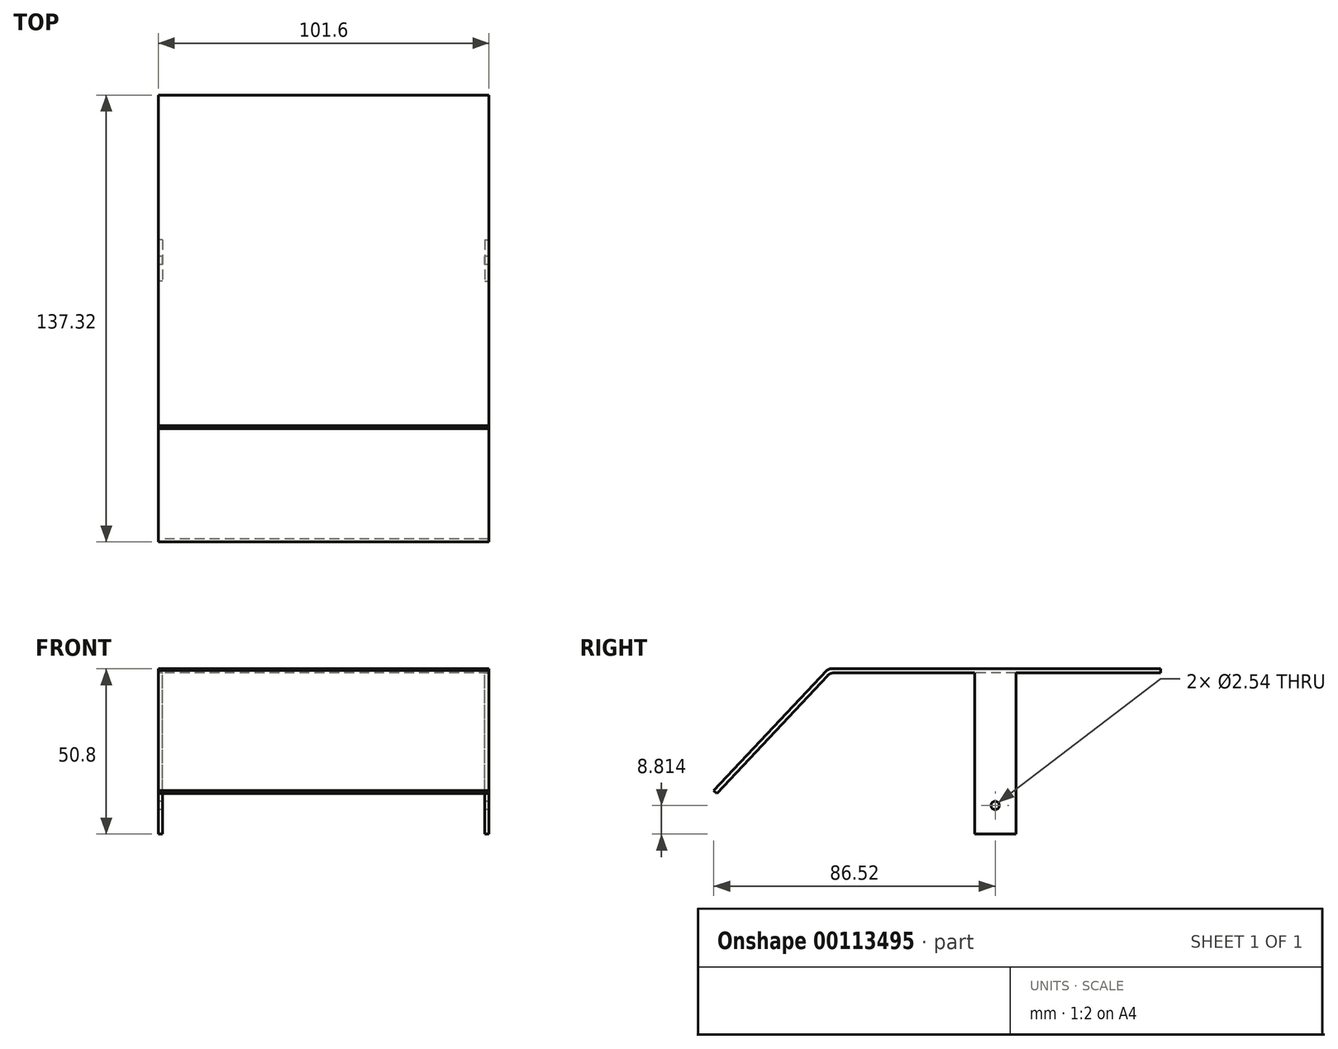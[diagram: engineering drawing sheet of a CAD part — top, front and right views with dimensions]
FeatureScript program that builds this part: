
annotation { "Feature Type Name" : "Feature", "Feature Type Description" : "" }
export const myFeature = defineFeature(function(context is Context, id is Id, definition is map)
    precondition{}
    {
        {
            var Q0;
            Q0=qCreatedBy(makeId("Top.planeOp"),FACE);
            var sketch = newSketch(context, id + "F0", { "sketchPlane" : qUnion([Q0])});
            skLineSegment(sketch, "E0.bottom", {"start": v(50.8, 50.8) * mm, "end": v(-50.8, 50.8) * mm});
            skLineSegment(sketch, "E0.top", {"start": v(50.8, -50.8) * mm, "end": v(-50.8, -50.8) * mm});
            skLineSegment(sketch, "E0.left", {"start": v(50.8, 50.8) * mm, "end": v(50.8, -50.8) * mm});
            skLineSegment(sketch, "E0.right", {"start": v(-50.8, 50.8) * mm, "end": v(-50.8, -50.8) * mm});
            skPoint(sketch, "E0.middle", {"position": v(0, 0) * mm});
            skSolve(sketch);
        }
        {
            var Q0;
            Q0=makeQuery(id+"F0.imprint","IMPRINT",FACE,{"disambiguationData":[TD([[makeQuery(id+"F0.imprint","IMPRINT",EDGE,{"derivedFrom":sQuery(id+"F0.wireOp",EDGE,"E0.bottom")}),1.0]])]});
            extrude(context, id + "F1", {"entities" : qUnion([Q0]), "depth" : 1.27 * mm});
        }
        {
            var Q0;
            Q0=qCreatedBy(makeId("Right.planeOp"),FACE);
            var sketch = newSketch(context, id + "F2", { "sketchPlane" : qUnion([Q0])});
            skLineSegment(sketch, "E1", {"start": v(-50.8, 0) * mm, "end": v(-85.6, -37.01) * mm});
            skLineSegment(sketch, "E2", {"start": v(-68.2, -18.5) * mm, "end": v(-69.12, -17.64) * mm});
            skLineSegment(sketch, "E3", {"start": v(-50.8, 0) * mm, "end": v(-51.73, 0.87) * mm});
            skLineSegment(sketch, "E4", {"start": v(-85.6, -37.01) * mm, "end": v(-86.52, -36.14) * mm});
            skLineSegment(sketch, "E5", {"start": v(-51.73, 0.87) * mm, "end": v(-86.52, -36.14) * mm});
            skLineSegment(sketch, "E6", {"start": v(-51.73, 0.87) * mm, "end": v(-50.8, 1.27) * mm});
            skLineSegment(sketch, "E7", {"start": v(-50.8, 1.27) * mm, "end": v(-50.8, 0) * mm});
            skSolve(sketch);
        }
        {
            var Q0;
            {var subQ2=sQuery(id+"F2.wireOp",EDGE,"E2");Q0=makeQuery(id+"F2.imprint","IMPRINT",FACE,{"disambiguationData":[TD([[makeQuery(id+"F2.imprint","IMPRINT",EDGE,{"derivedFrom":subQ2}),-1.0]])]});}
            var Q1;
            {var subQ2=sQuery(id+"F2.wireOp",EDGE,"E2");Q1=makeQuery(id+"F2.imprint","IMPRINT",FACE,{"disambiguationData":[TD([[makeQuery(id+"F2.imprint","IMPRINT",EDGE,{"derivedFrom":subQ2}),1.0]])]});}
            var Q2;
            Q2=makeQuery(id+"F2.imprint","IMPRINT",FACE,{"disambiguationData":[TD([[makeQuery(id+"F2.imprint","IMPRINT",EDGE,{"derivedFrom":sQuery(id+"F2.wireOp",EDGE,"E3")}),-1.0]])]});
            extrude(context, id + "F3", {"entities" : qUnion([Q0, Q1, Q2]), "operationType" : NewBodyOperationType.ADD, "depth" : 50.8 * mm, "hasSecondDirection" : true, "secondDirectionOppositeDirection" : true, "secondDirectionDepth" : 50.8 * mm});
        }
        {
            var Q0;
            Q0=makeQuery(id+"F1.opExtrude","SWEPT_FACE",FACE,{"disambiguationData":[OSD([sQuery(id+"F0.wireOp",EDGE,"E0.right")])]});
            var sketch = newSketch(context, id + "F4", { "sketchPlane" : qUnion([Q0])});
            skLineSegment(sketch, "E8.bottom", {"start": v(-6.35, -49.53) * mm, "end": v(6.35, -49.53) * mm});
            skLineSegment(sketch, "E8.top", {"start": v(-6.35, 1.27) * mm, "end": v(6.35, 1.27) * mm});
            skLineSegment(sketch, "E8.left", {"start": v(-6.35, -49.53) * mm, "end": v(-6.35, 1.27) * mm});
            skLineSegment(sketch, "E8.right", {"start": v(6.35, -49.53) * mm, "end": v(6.35, 1.27) * mm});
            skLineSegment(sketch, "E9", {"start": v(0, 0) * mm, "end": v(0, -69.8) * mm, "construction": true});
            skSolve(sketch);
        }
        {
            var Q0;
            {var subQ0=sQuery(id+"F4.wireOp",EDGE,"E8.bottom");Q0=makeQuery(id+"F4.imprint","IMPRINT",FACE,{"disambiguationData":[TD([[makeQuery(id+"F4.imprint","IMPRINT",EDGE,{"derivedFrom":subQ0}),1.0]])]});}
            extrude(context, id + "F5", {"entities" : qUnion([Q0]), "oppositeDirection" : true, "depth" : 1.27 * mm});
        }
        {
            var Q0;
            Q0=makeQuery(id+"F5.opExtrude","SWEPT_BODY",BODY,{"disambiguationData":[OSD([sQuery(id+"F0.wireOp",EDGE,"E0.right"),sQuery(id+"F4.wireOp",EDGE,"E8.bottom"),sQuery(id+"F4.wireOp",EDGE,"E8.left"),sQuery(id+"F4.wireOp",EDGE,"E8.right")])]});
            var Q1;
            Q1=qCreatedBy(makeId("Right.planeOp"),FACE);
            mirror(context, id + "F6", {"operationType" : NewBodyOperationType.ADD, "entities" : qUnion([Q0]), "mirrorPlane" : qUnion([Q1])});
        }
        {
            var Q0;
            {var subQ0=sQuery(id+"F0.wireOp",EDGE,"E0.right");Q0=makeQuery(id+"F6.boolean.opBoolean","MERGE",FACE,{"derivedFrom":[makeQuery(id+"F3.boolean.opBoolean","MERGE",FACE,{"derivedFrom":[makeQuery(id+"F1.opExtrude","SWEPT_FACE",FACE,{"disambiguationData":[OSD([subQ0])]}),makeQuery(id+"F3.opExtrude","CAP_FACE",FACE,{"disambiguationData":[OSD([sQuery(id+"F2.wireOp",EDGE,"E1"),sQuery(id+"F2.wireOp",EDGE,"E4"),sQuery(id+"F2.wireOp",EDGE,"E5"),sQuery(id+"F2.wireOp",EDGE,"E6"),sQuery(id+"F2.wireOp",EDGE,"E7")])],"isStart":true})]}),makeQuery(id+"F5.opExtrude","CAP_FACE",FACE,{"disambiguationData":[OSD([subQ0,sQuery(id+"F4.wireOp",EDGE,"E8.bottom"),sQuery(id+"F4.wireOp",EDGE,"E8.left"),sQuery(id+"F4.wireOp",EDGE,"E8.right")])],"isStart":true})]});}
            var sketch = newSketch(context, id + "F7", { "sketchPlane" : qUnion([Q0])});
            skCircle(sketch, "E10", {"center": v(0, -40.72) * mm, "radius": 1.27 * mm});
            skSolve(sketch);
        }
        {
            var Q0;
            Q0=sQuery(id+"F7.wireOp",VERTEX,"E10.center");
            var Q1;
            Q1=makeQuery(id+"F1.opExtrude","SWEPT_BODY",BODY,{"disambiguationData":[OSD([sQuery(id+"F0.wireOp",EDGE,"E0.bottom"),sQuery(id+"F0.wireOp",EDGE,"E0.top"),sQuery(id+"F0.wireOp",EDGE,"E0.left"),sQuery(id+"F0.wireOp",EDGE,"E0.right")])]});
            hole(context, id + "F8", {"style" : HoleStyle.SIMPLE, "endStyle" : HoleEndStyle.THROUGH, "holeDiameter" : 2.54 * mm, "locations" : qUnion([Q0]), "scope" : qUnion([Q1]), "isTappedThrough" : true});
        }
        {
            var Q0;
            Q0=makeQuery(id+"F3.boolean.opBoolean","MERGE",EDGE,{"derivedFrom":[makeQuery(id+"F1.opExtrude","CAP_EDGE",EDGE,{"disambiguationData":[OSD([sQuery(id+"F0.wireOp",EDGE,"E0.top")])],"isStart":true}),makeQuery(id+"F3.opExtrude","SWEPT_EDGE",EDGE,{"disambiguationData":[OSD([sQuery(id+"F2.wireOp",EDGE,"E1"),sQuery(id+"F2.wireOp",EDGE,"E3"),sQuery(id+"F2.wireOp",EDGE,"E7")])]})]});
            fillet(context, id + "F9", {"entities" : qUnion([Q0]), "radius" : 2.54 * mm, "tangentPropagation" : true, "allowEdgeOverflow" : false});
        }
    });
